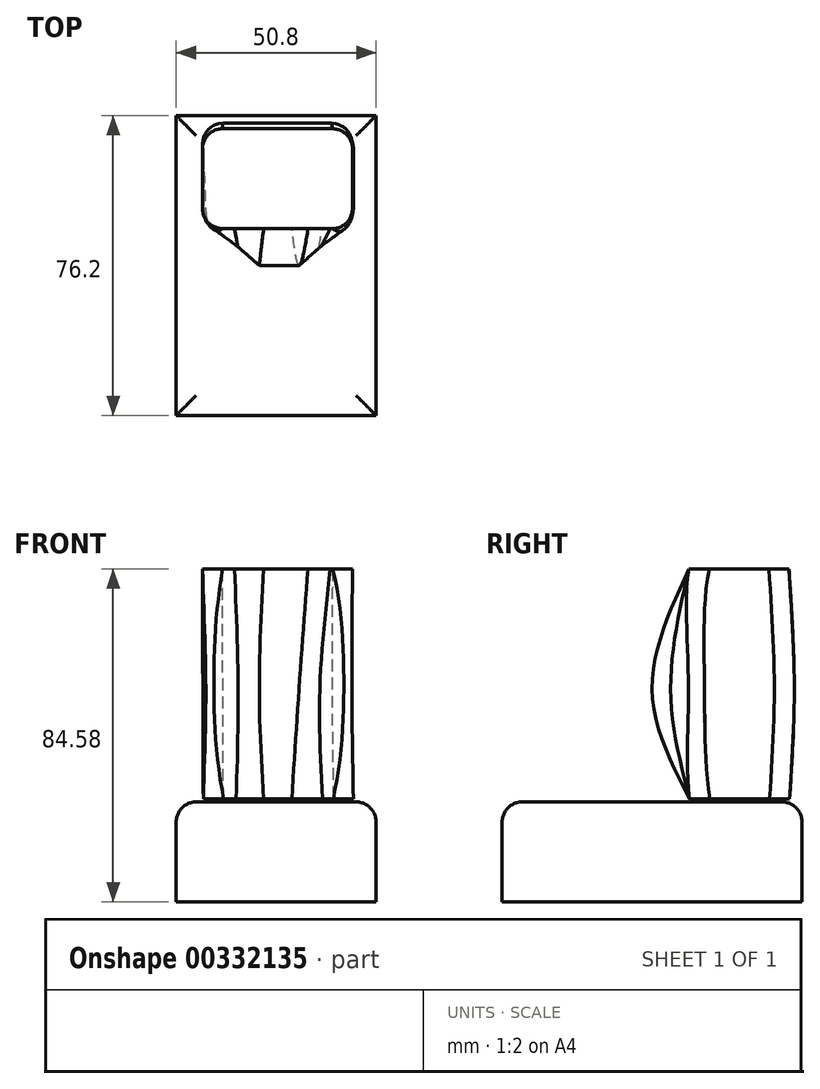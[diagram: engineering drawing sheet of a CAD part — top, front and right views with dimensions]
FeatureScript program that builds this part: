
annotation { "Feature Type Name" : "Feature", "Feature Type Description" : "" }
export const myFeature = defineFeature(function(context is Context, id is Id, definition is map)
    precondition{}
    {
        {
            var Q0;
            Q0=qCreatedBy(makeId("Top.planeOp"),FACE);
            cPlane(context, id + "F0", {"entities" : qUnion([Q0]), "cplaneType" : CPlaneType.OFFSET, "offset" : 110.49 * mm, "oppositeDirection" : true, "width" : 152.4 * mm, "height" : 152.4 * mm});
        }
        {
            var Q0;
            Q0=qCreatedBy(id+"F0.planeOp",FACE);
            var sketch = newSketch(context, id + "F1", { "sketchPlane" : qUnion([Q0])});
            skLineSegment(sketch, "E0.bottom", {"start": v(-26.29, 37.96) * mm, "end": v(24.51, 37.96) * mm});
            skLineSegment(sketch, "E0.top", {"start": v(-26.29, -38.24) * mm, "end": v(24.51, -38.24) * mm});
            skLineSegment(sketch, "E0.left", {"start": v(-26.29, 37.96) * mm, "end": v(-26.29, -38.24) * mm});
            skLineSegment(sketch, "E0.right", {"start": v(24.51, 37.96) * mm, "end": v(24.51, -38.24) * mm});
            skSolve(sketch);
        }
        {
            var Q0;
            Q0=makeQuery(id+"F1.imprint","IMPRINT",FACE,{"disambiguationData":[TD([[makeQuery(id+"F1.imprint","IMPRINT",EDGE,{"derivedFrom":sQuery(id+"F1.wireOp",EDGE,"E0.bottom")}),-1.0]])]});
            extrude(context, id + "F2", {"entities" : qUnion([Q0]), "depth" : 25.4 * mm});
        }
        {
            var Q0;
            Q0=makeQuery(id+"F2.opExtrude","CAP_EDGE",EDGE,{"disambiguationData":[OSD([sQuery(id+"F1.wireOp",EDGE,"E0.top")])],"isStart":false});
            var Q1;
            Q1=makeQuery(id+"F2.opExtrude","CAP_EDGE",EDGE,{"disambiguationData":[OSD([sQuery(id+"F1.wireOp",EDGE,"E0.right")])],"isStart":false});
            var Q2;
            Q2=makeQuery(id+"F2.opExtrude","CAP_EDGE",EDGE,{"disambiguationData":[OSD([sQuery(id+"F1.wireOp",EDGE,"E0.bottom")])],"isStart":false});
            var Q3;
            Q3=makeQuery(id+"F2.opExtrude","CAP_EDGE",EDGE,{"disambiguationData":[OSD([sQuery(id+"F1.wireOp",EDGE,"E0.left")])],"isStart":false});
            fillet(context, id + "F3", {"entities" : qUnion([Q0, Q1, Q2, Q3]), "radius" : 5.08 * mm, "tangentPropagation" : true, "allowEdgeOverflow" : false});
        }
        {
            var Q0;
            Q0=qCreatedBy(id+"F0.planeOp",FACE);
            cPlane(context, id + "F4", {"entities" : qUnion([Q0]), "cplaneType" : CPlaneType.OFFSET, "offset" : 26.16 * mm, "width" : 152.4 * mm, "height" : 152.4 * mm});
        }
        {
            var Q0;
            Q0=qCreatedBy(id+"F4.planeOp",FACE);
            cPlane(context, id + "F5", {"entities" : qUnion([Q0]), "cplaneType" : CPlaneType.OFFSET, "offset" : 58.42 * mm, "width" : 152.4 * mm, "height" : 152.4 * mm});
        }
        {
            var Q0;
            Q0=qCreatedBy(id+"F4.planeOp",FACE);
            cPlane(context, id + "F6", {"entities" : qUnion([Q0]), "cplaneType" : CPlaneType.OFFSET, "offset" : 25.4 * mm, "width" : 152.4 * mm, "height" : 152.4 * mm});
        }
        {
            var Q0;
            Q0=qCreatedBy(id+"F4.planeOp",FACE);
            var sketch = newSketch(context, id + "F7", { "sketchPlane" : qUnion([Q0])});
            skLineSegment(sketch, "E1.bottom", {"start": v(-19.38, 34.8) * mm, "end": v(18.72, 34.8) * mm});
            skLineSegment(sketch, "E1.top", {"start": v(-19.38, 9.4) * mm, "end": v(-11.04, 9.4) * mm});
            skLineSegment(sketch, "E1.left", {"start": v(-19.38, 34.8) * mm, "end": v(-19.38, 9.4) * mm});
            skLineSegment(sketch, "E1.right", {"start": v(18.72, 34.8) * mm, "end": v(18.72, 9.4) * mm});
            skLineSegment(sketch, "E2", {"start": v(-11.04, 9.4) * mm, "end": v(-4.07, 9.4) * mm});
            skLineSegment(sketch, "E3", {"start": v(-4.07, 9.4) * mm, "end": v(3.1, 9.4) * mm});
            skLineSegment(sketch, "E4", {"start": v(3.1, 9.4) * mm, "end": v(10.9, 9.4) * mm});
            skLineSegment(sketch, "E5", {"start": v(10.9, 9.4) * mm, "end": v(18.72, 9.4) * mm});
            skSolve(sketch);
        }
        {
            var Q0;
            Q0=qCreatedBy(id+"F6.planeOp",FACE);
            var sketch = newSketch(context, id + "F8", { "sketchPlane" : qUnion([Q0])});
            skLineSegment(sketch, "E6", {"start": v(-19.73, 36) * mm, "end": v(18.37, 36) * mm});
            skLineSegment(sketch, "E7", {"start": v(18.37, 36) * mm, "end": v(18.37, 10.6) * mm});
            skLineSegment(sketch, "E8", {"start": v(18.37, 10.6) * mm, "end": v(10.14, 4.64) * mm});
            skLineSegment(sketch, "E9", {"start": v(10.14, 4.64) * mm, "end": v(4.75, 0) * mm});
            skLineSegment(sketch, "E10", {"start": v(4.75, 0) * mm, "end": v(-5.15, 0) * mm});
            skLineSegment(sketch, "E11", {"start": v(-5.15, 0) * mm, "end": v(-10.54, 4.64) * mm});
            skLineSegment(sketch, "E12", {"start": v(-10.54, 4.64) * mm, "end": v(-18.66, 10.6) * mm});
            skLineSegment(sketch, "E13", {"start": v(-18.66, 10.6) * mm, "end": v(-19.73, 36) * mm});
            skSolve(sketch);
        }
        {
            var Q0;
            Q0=qCreatedBy(id+"F5.planeOp",FACE);
            var sketch = newSketch(context, id + "F9", { "sketchPlane" : qUnion([Q0])});
            skLineSegment(sketch, "E14.bottom", {"start": v(-19.6, 34.63) * mm, "end": v(18.5, 34.63) * mm});
            skLineSegment(sketch, "E14.top", {"start": v(-19.6, 9.23) * mm, "end": v(-11.47, 9.23) * mm});
            skLineSegment(sketch, "E14.left", {"start": v(-19.6, 34.63) * mm, "end": v(-19.6, 9.23) * mm});
            skLineSegment(sketch, "E14.right", {"start": v(18.5, 34.63) * mm, "end": v(18.5, 9.23) * mm});
            skLineSegment(sketch, "E15", {"start": v(-11.47, 9.23) * mm, "end": v(-4.08, 9.23) * mm});
            skLineSegment(sketch, "E16", {"start": v(-4.08, 9.23) * mm, "end": v(7.2, 9.23) * mm});
            skLineSegment(sketch, "E17", {"start": v(7.2, 9.23) * mm, "end": v(12.85, 9.23) * mm});
            skLineSegment(sketch, "E18", {"start": v(12.85, 9.23) * mm, "end": v(18.5, 9.23) * mm});
            skSolve(sketch);
        }
        {
            var Q0;
            Q0=makeQuery(id+"F9.imprint","IMPRINT",FACE,{"disambiguationData":[TD([[makeQuery(id+"F9.imprint","IMPRINT",EDGE,{"derivedFrom":sQuery(id+"F9.wireOp",EDGE,"E14.bottom")}),-1.0]])]});
            var Q1;
            Q1=makeQuery(id+"F8.imprint","IMPRINT",FACE,{"disambiguationData":[TD([[makeQuery(id+"F8.imprint","IMPRINT",EDGE,{"derivedFrom":sQuery(id+"F8.wireOp",EDGE,"E6")}),-1.0]])]});
            var Q2;
            Q2=makeQuery(id+"F7.imprint","IMPRINT",FACE,{"disambiguationData":[TD([[makeQuery(id+"F7.imprint","IMPRINT",EDGE,{"derivedFrom":sQuery(id+"F7.wireOp",EDGE,"E1.bottom")}),-1.0]])]});
            loft(context, id + "F10", {"sheetProfilesArray" : [{ "sheetProfileEntities" : qUnion([Q0]) }, { "sheetProfileEntities" : qUnion([Q1]) }, { "sheetProfileEntities" : qUnion([Q2]) }]});
        }
        {
            var Q0;
            Q0=makeQuery(id+"F10.opLoft","SWEPT_EDGE",EDGE,{"disambiguationData":[OSD([sQuery(id+"F8.wireOp",EDGE,"E7"),sQuery(id+"F8.wireOp",EDGE,"E8"),sQuery(id+"F9.wireOp",EDGE,"E14.right"),sQuery(id+"F9.wireOp",EDGE,"E18")])]});
            var Q1;
            Q1=makeQuery(id+"F10.opLoft","SWEPT_EDGE",EDGE,{"disambiguationData":[OSD([sQuery(id+"F8.wireOp",EDGE,"E6"),sQuery(id+"F8.wireOp",EDGE,"E7"),sQuery(id+"F9.wireOp",EDGE,"E14.bottom"),sQuery(id+"F9.wireOp",EDGE,"E14.right")])]});
            var Q2;
            Q2=makeQuery(id+"F10.opLoft","SWEPT_EDGE",EDGE,{"disambiguationData":[OSD([sQuery(id+"F8.wireOp",EDGE,"E12"),sQuery(id+"F8.wireOp",EDGE,"E13"),sQuery(id+"F9.wireOp",EDGE,"E14.top"),sQuery(id+"F9.wireOp",EDGE,"E14.left")])]});
            var Q3;
            Q3=makeQuery(id+"F10.opLoft","SWEPT_EDGE",EDGE,{"disambiguationData":[OSD([sQuery(id+"F8.wireOp",EDGE,"E6"),sQuery(id+"F8.wireOp",EDGE,"E13"),sQuery(id+"F9.wireOp",EDGE,"E14.bottom"),sQuery(id+"F9.wireOp",EDGE,"E14.left")])]});
            fillet(context, id + "F11", {"entities" : qUnion([Q0, Q1, Q2, Q3]), "radius" : 5.08 * mm, "tangentPropagation" : true, "allowEdgeOverflow" : false});
        }
    });
